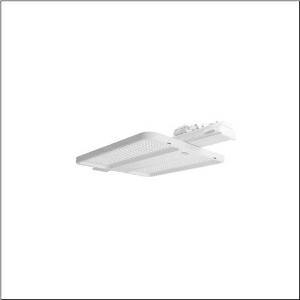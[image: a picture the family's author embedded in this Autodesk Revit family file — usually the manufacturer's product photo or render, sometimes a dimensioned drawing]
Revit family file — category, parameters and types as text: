
# Revit family: highbay_11_fur_licross_r__tragschiene_midi_51hn11da4fla01_ee5a
name_source: partatom
category: Lighting Fixtures
units: mm (PartAtom-declared; Revit-internal decimal feet)

## family parameters
Cut with Voids When Loaded = No
Host = Face
Light Source = No
Part Type = Normal
Room Calculation Point = No
Round Connector Dimension = Use Diameter
Shared = No

## types (1)
- --- (1 x LED, 15000 lm, 73.7 W, 4000K)
    Apparent Load = 74 VA
    CIE Flux Codes = 85 97 100 100 100
    Color Rendering = 80
    Color Temperature = 4000K
    Default Elevation = 1800 mm
    Description = high bay luminaire Highbay 11 for Licross® trunking rail midi; direct symmetric narrow distribution, light control with lens of PMMA; UGR ≤ 22 (X = 4H | Y = 8H | S = 0.25H | reflection values 70/50/20); luminous flux: 15.000lm; light colour: 840, colour temperature: 4000K, MacAdam ≤ 2 SDCM (initial), colour rendering: CRI > 80; luminous efficacy: 203,5lm/W; rated service life: 100.000h (L95/B50) at AT= 25°C; control: Bluetooth® Mesh; for wireless networking: Node multi-sensor luminaire for setting up a local control solution without a higher-level application controller, intelligence completely integrated into the luminaire; with auto-swarm function: leading lighting creates safety. The function is already active without any „out-of-the-box“ commissioning; commissioning is not necessary thanks to „out-of-the-box“ functions: basic functions (presence lighting, follow-up times, fading times, etc.) are already preset at the factory; no control line such as DALI between the Node multi-sensor luminaires and Nodes is required, wireless integration of other Node luminaires and Node multi-sensor luminaires into the network is possible; number of Node multi-sensor luminaires in the project can be expanded as required, network sizes > 300 Nodes can be realized; can also be connected to lighting or building automation via various gateways upon request; integrated DALI2 ECG provides luminaire data (according to IEC62386, Part 251), energy data (Part 252), and monitoring and analytics data (Part 253) to higher-level systems for further processing; luminaire with PIR sensor (passive-infrared); with light sensor; luminaire connection: plug, 5-pole, with phase selectionmains connection: 230..240V, AC 50/60Hz; connected load: 73,7W; protection rating (complete): IP64; insulation class (complete): insulation class I (protective earthing); protection symbol: D; certification: CE, ENEC, VDE, UKCA; internal wiring halogen-free; luminaire LABS conformity tested according to VDMA 24364:2018-05; corresponds to IFS (International Featured Standards) requirements for safety and quality in the food industry; housing frame of high-performance plastic PA6, matt traffic white (RAL 9016); cover of PMMA; fixing on rail side of steel, galvanised, white; blank cover of PC/ABS, traffic white (RAL 9016); dimension (LxWxH): 750 x 442 x 72mm; permissible operating ambient temperature: -20..+40°C (reducing of maximum allowable ambient temperature of 5°C with ceiling mounting); packaging unit: 1 piece
    Height = 72 mm  [stored 0.23622 ft]
    Lamp = 1 x LED
    Lamp Light Flux = 15000 lm
    Lamp Power = 73.7 W
    Lamp count = 1
    Length = 474 mm
    Luminous efficacy = 204 lm/W
    Manufacturer = Siteco
    ModVariant = No
    Model = 51HN11DA4FLA01
    Mounting Place = Ceiling
    Mounting Type = Pendant
    Number of Poles = 1
    OnlyDefault = Yes
    Power Factor = 1
    Product Name = Highbay 11 für Licross® Tragschiene midi
    Product group = high bay luminaire
    ProductGroupID = 901
    Protection Class = Protection class I
    Protection Degree = IP 64
    RLX_Detail_Level = 1
    RLX_Emergency_Light_Flux = 0 lm
    RLX_Emergency_Type = 0
    RLX_Emergency_Type_DB = No
    RlxData = <blob elided: 18401 chars, md5=e6b64bdb>
    Socket = socket
    Standby Power = 0 W
    System Light Flux = 15000 lm
    System Power = 74 W
    Type Comments = factory setting: luminous flux: 100 % | dim-lin: 254 | 339 mA
    Type Image = l_1363262.jpg
    URL = http://relux.com
    VarID = @adj_022377
    Voltage = 0 V
    Weight = 0.00 kg
    Width = 442 mm

note: [stored X ft] marks values corroborated as IEEE doubles in the binary element streams (Revit-internal decimal feet)

## geometry (parser evidence)
native form markers: Blend x4, Sweep x13
no freeform markers — native parametric forms only
